# Revit family: QF_COMENDA_6G3170_6G3190_1155 H_6G3277_CAT
name_source: partatom
category: Attrezzature speciali
units: mm (PartAtom-declared; Revit-internal decimal feet)

## family parameters
Basato su piano di lavoro = No
Condiviso = No
Numero OmniClass = 23.40.40.14
Punto di calcolo locali = No
Quota connettore circolare = Usa diametro
Sempre verticale = Sì
Taglio con vuoti quando caricato = No
Tipo di parte = Normale
Titolo OmniClass = Food Service Equipment

## types (4) — shared parameters
Altezza da terra raccordo acqua calda = 175 mm  [stored 0.574147 ft]
Altezza dello scarico diretto acqua da pavimento finito = 145 mm  [stored 0.475722 ft]
Corrente di funzionamento normale = 23 A
Diametro dello scarico diretto di acqua = 1 1/2"
Diametro raccordo acqua calda = 1"
Fase = 3
Frequenza = 50 Hz
Lunghezza = 1530 mm  [stored 5.01969 ft]
Numero dei poli = 3
Peso netto = 270.00 kg
Potenza elettrica = 15000 W
Pressione minima acqua calda = 2000.0 Pa
Produttore = COMENDA
Protezione contro le sovracorrenti = 32 A
Temperatura raccomandata per acqua calda = 50 °C
Tensione = 400 V
URL = www.comenda.eu
zero-valued in all types: Prospetto di default

## per-type parameters (varying)
| type | Altezza | Altezza allacciamento elettrico da pavimento finito | Descrizione | Modello | Profondità | URL catalogo |
| 6G3190 | 1870 mm | 135 mm  [stored 0.442913 ft] | THREE-PHASE FRONT LOADING POTWASHER WITH RCD | G-EVO 1155 R RCD | 900 mm  [stored 2.95276 ft] | https://comenda.eu |
| 6G3170 | 1870 mm | 135 mm  [stored 0.442913 ft] | THREE-PHASE FRONT LOADING POTWASHER  WITH RCD | G-EVO 1005 R RCD | 870 mm  [stored 2.85433 ft] | https://comenda.eu |
| 6G3277 | 2020 mm  [stored 6.6273 ft] | 135 mm  [stored 0.442913 ft] | THREE-PHASE FRONT LOADING POTWASHER WITH RCD | G-EVO 1005 H RCD | 900 mm  [stored 2.95276 ft] | /comenda.eu/wp-content/uploads/2024/02/Scheda-tecnica_G-EVO-1005-R_15.02.2024_ITA.pdf |
| G-EVO 1155 H | 2020 mm  [stored 6.6273 ft] | 134 mm | THREE-PHASE FRONT LOADING POTWASHER WITH RCD | G-EVO 1155 H R RCD | 900 mm  [stored 2.95276 ft] | https://comenda.eu |

note: [stored X ft] marks values corroborated as IEEE doubles in the binary element streams (Revit-internal decimal feet)

## geometry (parser evidence)
native form markers: Sweep x4
no freeform markers — native parametric forms only
